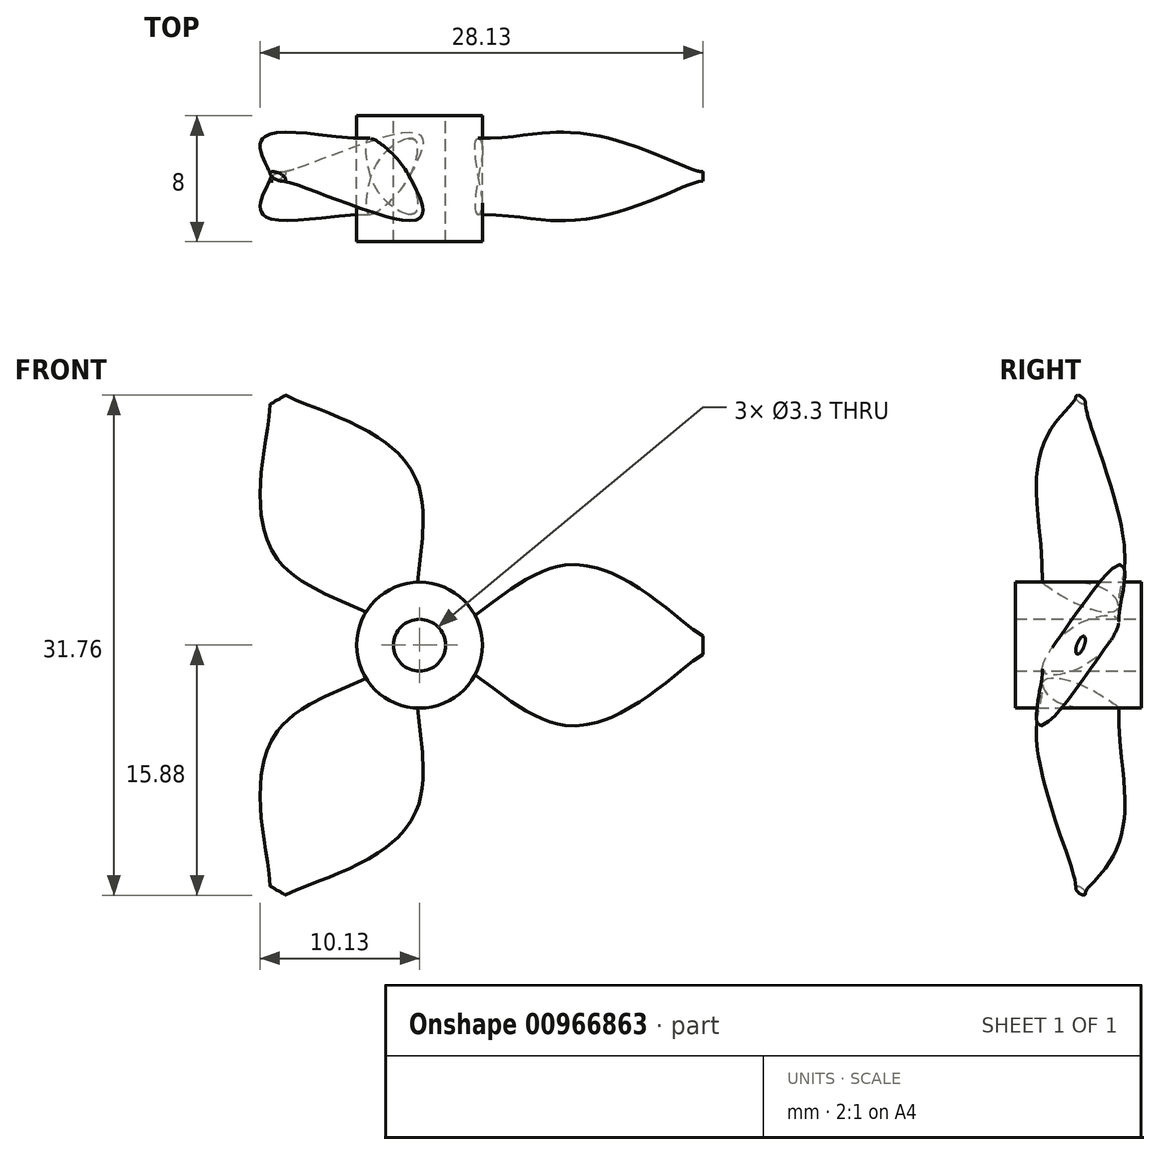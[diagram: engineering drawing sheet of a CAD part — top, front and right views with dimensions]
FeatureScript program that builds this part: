
annotation { "Feature Type Name" : "Feature", "Feature Type Description" : "" }
export const myFeature = defineFeature(function(context is Context, id is Id, definition is map)
    precondition{}
    {
        {
            var Q0;
            Q0=qCreatedBy(makeId("Front.planeOp"),FACE);
            var sketch = newSketch(context, id + "F0", { "sketchPlane" : qUnion([Q0])});
            skCircle(sketch, "E0", {"center": v(0, 0) * mm, "radius": 4 * mm});
            skCircle(sketch, "E1", {"center": v(0, 0) * mm, "radius": 1.65 * mm});
            skSolve(sketch);
        }
        {
            var Q0;
            Q0=makeQuery(id+"F0.imprint","IMPRINT",FACE,{"disambiguationData":[TD([[makeQuery(id+"F0.imprint","IMPRINT",EDGE,{"derivedFrom":sQuery(id+"F0.wireOp",EDGE,"E0")}),1.0]])]});
            extrude(context, id + "F1", {"entities" : qUnion([Q0]), "depth" : 8 * mm, "offsetDistance" : 25 * mm});
        }
        {
            var Q0;
            Q0=qCreatedBy(makeId("Right.planeOp"),FACE);
            cPlane(context, id + "F2", {"entities" : qUnion([Q0]), "cplaneType" : CPlaneType.OFFSET, "offset" : 2.75 * mm, "width" : 150 * mm, "height" : 150 * mm});
        }
        {
            var Q0;
            Q0=qCreatedBy(id+"F2.planeOp",FACE);
            var sketch = newSketch(context, id + "F3", { "sketchPlane" : qUnion([Q0])});
            skEllipse(sketch, "E2", {"center": v(-3.86, 0) * mm, "majorRadius": 2.8 * mm, "minorRadius": 0.7 * mm, "majorAxis": v(0.88, 0.47)});
            skSolve(sketch);
        }
        {
            var Q0;
            Q0=qCreatedBy(makeId("Right.planeOp"),FACE);
            cPlane(context, id + "F4", {"entities" : qUnion([Q0]), "cplaneType" : CPlaneType.OFFSET, "offset" : 9 * mm, "width" : 150 * mm, "height" : 150 * mm});
        }
        {
            var Q0;
            Q0=qCreatedBy(id+"F4.planeOp",FACE);
            var sketch = newSketch(context, id + "F5", { "sketchPlane" : qUnion([Q0])});
            skEllipse(sketch, "E3", {"center": v(-3.86, 0) * mm, "majorRadius": 5.67 * mm, "minorRadius": 1.12 * mm, "majorAxis": v(0.46, 0.89)});
            skSolve(sketch);
        }
        {
            var Q0;
            Q0=qCreatedBy(makeId("Right.planeOp"),FACE);
            cPlane(context, id + "F6", {"entities" : qUnion([Q0]), "cplaneType" : CPlaneType.OFFSET, "offset" : 18 * mm, "width" : 150 * mm, "height" : 150 * mm});
        }
        {
            var Q0;
            Q0=qCreatedBy(id+"F6.planeOp",FACE);
            var sketch = newSketch(context, id + "F7", { "sketchPlane" : qUnion([Q0])});
            skEllipse(sketch, "E4", {"center": v(-3.86, 0) * mm, "majorRadius": 0.6 * mm, "minorRadius": 0.23 * mm, "majorAxis": v(0.36, 0.93)});
            skSolve(sketch);
        }
        {
            var Q1;
            Q1 = qSketchRegion(id + "F3", true);
            var Q2;
            Q2 = qSketchRegion(id + "F5", true);
            var Q3;
            Q3 = qSketchRegion(id + "F7", true);
            loft(context, id + "F8", {"operationType" : NewBodyOperationType.ADD, "sheetProfilesArray" : [{ "sheetProfileEntities" : qUnion([Q1]) }, { "sheetProfileEntities" : qUnion([Q2]) }, { "sheetProfileEntities" : qUnion([Q3]) }]});
        }
        {
            var Q0;
            Q0=qCreatedBy(makeId("Right.planeOp"),FACE);
            var sketch = newSketch(context, id + "F9", { "sketchPlane" : qUnion([Q0])});
            skLineSegment(sketch, "E5", {"start": v(0, 0) * mm, "end": v(-13.33, 0) * mm});
            skSolve(sketch);
        }
        {
            var Q0;
            Q0=makeQuery(id+"F1.opExtrude","SWEPT_BODY",BODY,{"disambiguationData":[OSD([sQuery(id+"F0.wireOp",EDGE,"E0"),sQuery(id+"F0.wireOp",EDGE,"E1")])]});
            var Q1;
            Q1=sQuery(id+"F9.wireOp",EDGE,"E5");
            circularPattern(context, id + "F10", {"entities" : qUnion([Q0]), "axis" : qUnion([Q1]), "angle" : 360 * degree, "instanceCount" : 3, "equalSpace" : true});
        }
    });
